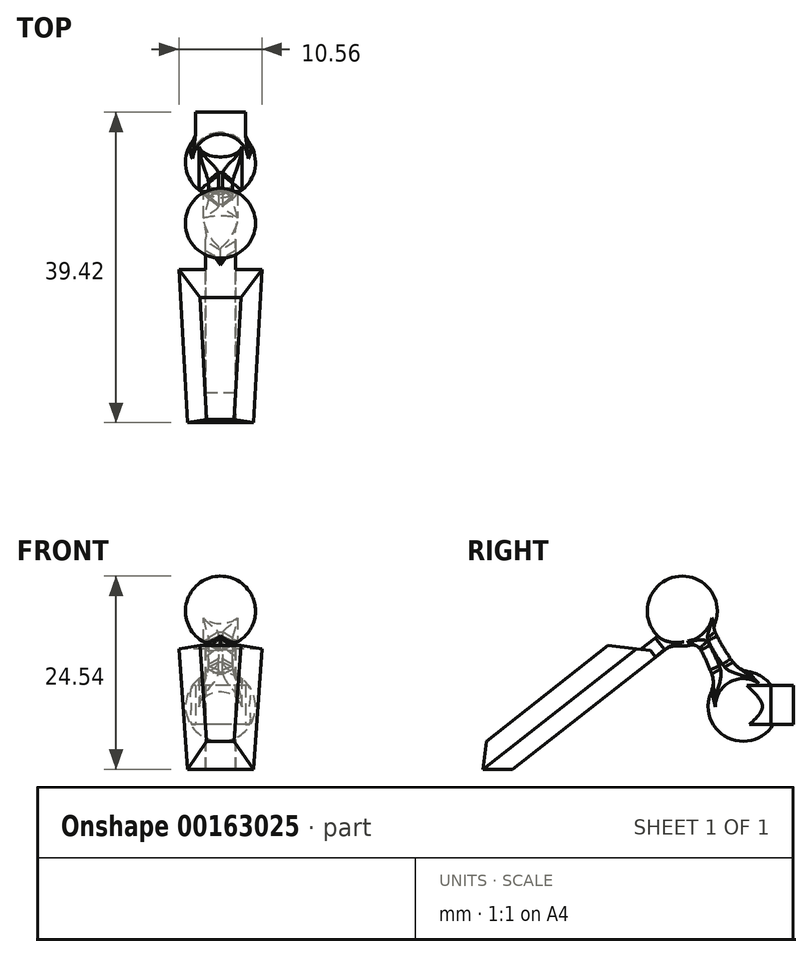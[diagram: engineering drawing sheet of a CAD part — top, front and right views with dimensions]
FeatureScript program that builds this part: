
annotation { "Feature Type Name" : "Feature", "Feature Type Description" : "" }
export const myFeature = defineFeature(function(context is Context, id is Id, definition is map)
    precondition{}
    {
        {
            var Q0;
            Q0=qCreatedBy(makeId("Right.planeOp"),FACE);
            var sketch = newSketch(context, id + "F0", { "sketchPlane" : qUnion([Q0])});
            skArc(sketch, "E0", {"start": v(4.45, 0) * mm, "mid": v(0, 4.45) * mm, "end": v(-4.45, 0) * mm});
            skLineSegment(sketch, "E1", {"start": v(-4.45, 0) * mm, "end": v(4.45, 0) * mm});
            skSolve(sketch);
        }
        {
            var Q0;
            Q0 = qSketchRegion(id + "F0", true);
            var Q1;
            Q1=sQuery(id+"F0.wireOp",EDGE,"E1");
            revolve(context, id + "F1", {"entities" : qUnion([Q0]), "axis" : qUnion([Q1]), "revolveType" : RevolveType.FULL});
        }
        {
            var Q0;
            Q0=qCreatedBy(makeId("Right.planeOp"),FACE);
            var sketch = newSketch(context, id + "F2", { "sketchPlane" : qUnion([Q0])});
            skArc(sketch, "E2", {"start": v(-3.29, 12.1) * mm, "mid": v(-7.73, 16.54) * mm, "end": v(-12.18, 12.1) * mm});
            skLineSegment(sketch, "E3", {"start": v(-16.01, 12.1) * mm, "end": v(-0.23, 12.1) * mm});
            skSolve(sketch);
        }
        {
            var Q0;
            Q0 = qSketchRegion(id + "F2", true);
            var Q1;
            Q1=sQuery(id+"F2.wireOp",EDGE,"E3");
            revolve(context, id + "F3", {"operationType" : NewBodyOperationType.ADD, "entities" : qUnion([Q0]), "axis" : qUnion([Q1]), "revolveType" : RevolveType.FULL});
        }
        {
            var Q0;
            Q0=qCreatedBy(makeId("Right.planeOp"),FACE);
            var sketch = newSketch(context, id + "F4", { "sketchPlane" : qUnion([Q0])});
            skLineSegment(sketch, "E4", {"start": v(0, 0) * mm, "end": v(-6.36, 11.76) * mm});
            skArc(sketch, "E5", {"start": v(-2.54, -2.6) * mm, "mid": v(-4.16, 4.59) * mm, "end": v(-7.92, 10.92) * mm});
            skArc(sketch, "E6.MirrorCS", {"start": v(3.56, 0.7) * mm, "mid": v(-1.56, 6) * mm, "end": v(-4.8, 12.6) * mm});
            skLineSegment(sketch, "E7", {"start": v(-2.54, -2.6) * mm, "end": v(3.56, 0.7) * mm});
            skLineSegment(sketch, "E8", {"start": v(-4.8, 12.6) * mm, "end": v(-7.92, 10.92) * mm});
            skPoint(sketch, "E9.orphan", {"position": v(-5.82, 18.71) * mm});
            skPoint(sketch, "E10.orphan", {"position": v(-12.46, 15.12) * mm});
            skSolve(sketch);
        }
        {
            var Q0;
            Q0 = qSketchRegion(id + "F4", true);
            extrude(context, id + "F5", {"entities" : qUnion([Q0]), "operationType" : NewBodyOperationType.ADD, "depth" : 3.05 * mm, "symmetric" : true});
        }
        {
            var Q0;
            Q0=qCreatedBy(makeId("Right.planeOp"),FACE);
            var sketch = newSketch(context, id + "F6", { "sketchPlane" : qUnion([Q0])});
            skLineSegment(sketch, "E11", {"start": v(-29.28, -8) * mm, "end": v(-7.9, 8.8) * mm});
            skLineSegment(sketch, "E12", {"start": v(-7.9, 8.8) * mm, "end": v(-9.42, 10.56) * mm});
            skLineSegment(sketch, "E13", {"start": v(-13.02, 7.73) * mm, "end": v(-33.05, -8) * mm});
            skLineSegment(sketch, "E14", {"start": v(-33.05, -8) * mm, "end": v(-29.28, -8) * mm});
            skLineSegment(sketch, "E15", {"start": v(-13.02, 7.73) * mm, "end": v(-9.42, 10.56) * mm});
            skSolve(sketch);
        }
        {
            var Q0;
            Q0 = qSketchRegion(id + "F6", true);
            extrude(context, id + "F7", {"entities" : qUnion([Q0]), "operationType" : NewBodyOperationType.ADD, "depth" : 3.8 * mm, "symmetric" : true});
        }
        {
            var Q0;
            Q0=qCreatedBy(makeId("Right.planeOp"),FACE);
            var sketch = newSketch(context, id + "F8", { "sketchPlane" : qUnion([Q0])});
            skLineSegment(sketch, "E16.bottom", {"start": v(3.52, -2.31) * mm, "end": v(6.37, -2.31) * mm});
            skLineSegment(sketch, "E16.top", {"start": v(3.52, 2.64) * mm, "end": v(6.37, 2.64) * mm});
            skLineSegment(sketch, "E16.left", {"start": v(3.52, -2.31) * mm, "end": v(3.52, 2.64) * mm});
            skLineSegment(sketch, "E17", {"start": v(6.37, 2.64) * mm, "end": v(6.37, -2.31) * mm});
            skSolve(sketch);
        }
        {
            var Q0;
            Q0 = qSketchRegion(id + "F8", true);
            extrude(context, id + "F9", {"entities" : qUnion([Q0]), "operationType" : NewBodyOperationType.ADD, "depth" : 3.17 * mm, "hasSecondDirection" : true, "secondDirectionOppositeDirection" : true, "secondDirectionDepth" : 3.17 * mm});
        }
        {
            var Q0;
            Q0=makeQuery(id+"F9.boolean.opBoolean","INTERSECT",EDGE,{"disambiguationData":[OD(1.0)],"derivedFrom":[makeQuery(id+"F1.opRevolve","SWEPT_FACE",FACE,{"disambiguationData":[OSD([sQuery(id+"F0.wireOp",EDGE,"E0")])]}),makeQuery(id+"F9.opExtrude","SWEPT_FACE",FACE,{"disambiguationData":[OSD([sQuery(id+"F8.wireOp",EDGE,"E16.left")])]})]});
            var Q1;
            Q1=makeQuery(id+"F9.boolean.opBoolean","INTERSECT",EDGE,{"disambiguationData":[OD(0.0)],"derivedFrom":[makeQuery(id+"F1.opRevolve","SWEPT_FACE",FACE,{"disambiguationData":[OSD([sQuery(id+"F0.wireOp",EDGE,"E0")])]}),makeQuery(id+"F9.opExtrude","SWEPT_FACE",FACE,{"disambiguationData":[OSD([sQuery(id+"F8.wireOp",EDGE,"E16.left")])]})]});
            fillet(context, id + "F10", {"entities" : qUnion([Q0, Q1]), "radius" : 5.08 * mm, "tangentPropagation" : true, "allowEdgeOverflow" : false});
        }
        {
            var Q0;
            Q0=makeQuery(id+"F5.boolean.opBoolean","INTERSECT",EDGE,{"derivedFrom":[makeQuery(id+"F1.opRevolve","SWEPT_FACE",FACE,{"disambiguationData":[OSD([sQuery(id+"F0.wireOp",EDGE,"E0")])]}),makeQuery(id+"F5.opExtrude","CAP_FACE",FACE,{"disambiguationData":[OSD([sQuery(id+"F4.wireOp",EDGE,"E5"),sQuery(id+"F4.wireOp",EDGE,"E6.MirrorCS"),sQuery(id+"F4.wireOp",EDGE,"E7"),sQuery(id+"F4.wireOp",EDGE,"5klLo1RB-Tudc-jpJ2-xB18-EwgxkBeXyRiw")])],"isStart":false})]});
            var Q1;
            Q1=makeQuery(id+"F5.boolean.opBoolean","INTERSECT",EDGE,{"derivedFrom":[makeQuery(id+"F1.opRevolve","SWEPT_FACE",FACE,{"disambiguationData":[OSD([sQuery(id+"F0.wireOp",EDGE,"E0")])]}),makeQuery(id+"F5.opExtrude","SWEPT_FACE",FACE,{"disambiguationData":[OSD([sQuery(id+"F4.wireOp",EDGE,"E6.MirrorCS")])]})]});
            var Q2;
            Q2=makeQuery(id+"F5.boolean.opBoolean","INTERSECT",EDGE,{"derivedFrom":[makeQuery(id+"F1.opRevolve","SWEPT_FACE",FACE,{"disambiguationData":[OSD([sQuery(id+"F0.wireOp",EDGE,"E0")])]}),makeQuery(id+"F5.opExtrude","CAP_FACE",FACE,{"disambiguationData":[OSD([sQuery(id+"F4.wireOp",EDGE,"E5"),sQuery(id+"F4.wireOp",EDGE,"E6.MirrorCS"),sQuery(id+"F4.wireOp",EDGE,"E7"),sQuery(id+"F4.wireOp",EDGE,"5klLo1RB-Tudc-jpJ2-xB18-EwgxkBeXyRiw")])],"isStart":true})]});
            var Q3;
            Q3=makeQuery(id+"F5.boolean.opBoolean","INTERSECT",EDGE,{"derivedFrom":[makeQuery(id+"F1.opRevolve","SWEPT_FACE",FACE,{"disambiguationData":[OSD([sQuery(id+"F0.wireOp",EDGE,"E0")])]}),makeQuery(id+"F5.opExtrude","SWEPT_FACE",FACE,{"disambiguationData":[OSD([sQuery(id+"F4.wireOp",EDGE,"E5")])]})]});
            fillet(context, id + "F11", {"entities" : qUnion([Q0, Q1, Q2, Q3]), "radius" : 3.05 * mm, "tangentPropagation" : true, "allowEdgeOverflow" : false});
        }
        {
            var Q0;
            Q0=makeQuery(id+"F5.boolean.opBoolean","INTERSECT",EDGE,{"derivedFrom":[makeQuery(id+"F3.opRevolve","SWEPT_FACE",FACE,{"disambiguationData":[OSD([sQuery(id+"F2.wireOp",EDGE,"E2")])]}),makeQuery(id+"F5.opExtrude","CAP_FACE",FACE,{"disambiguationData":[OSD([sQuery(id+"F4.wireOp",EDGE,"E5"),sQuery(id+"F4.wireOp",EDGE,"E6.MirrorCS"),sQuery(id+"F4.wireOp",EDGE,"E7"),sQuery(id+"F4.wireOp",EDGE,"5klLo1RB-Tudc-jpJ2-xB18-EwgxkBeXyRiw")])],"isStart":false})]});
            var Q1;
            Q1=makeQuery(id+"F5.boolean.opBoolean","INTERSECT",EDGE,{"derivedFrom":[makeQuery(id+"F3.opRevolve","SWEPT_FACE",FACE,{"disambiguationData":[OSD([sQuery(id+"F2.wireOp",EDGE,"E2")])]}),makeQuery(id+"F5.opExtrude","SWEPT_FACE",FACE,{"disambiguationData":[OSD([sQuery(id+"F4.wireOp",EDGE,"E6.MirrorCS")])]})]});
            var Q2;
            Q2=makeQuery(id+"F5.boolean.opBoolean","INTERSECT",EDGE,{"derivedFrom":[makeQuery(id+"F3.opRevolve","SWEPT_FACE",FACE,{"disambiguationData":[OSD([sQuery(id+"F2.wireOp",EDGE,"E2")])]}),makeQuery(id+"F5.opExtrude","CAP_FACE",FACE,{"disambiguationData":[OSD([sQuery(id+"F4.wireOp",EDGE,"E5"),sQuery(id+"F4.wireOp",EDGE,"E6.MirrorCS"),sQuery(id+"F4.wireOp",EDGE,"E7"),sQuery(id+"F4.wireOp",EDGE,"5klLo1RB-Tudc-jpJ2-xB18-EwgxkBeXyRiw")])],"isStart":true})]});
            var Q3;
            Q3=makeQuery(id+"F5.boolean.opBoolean","INTERSECT",EDGE,{"derivedFrom":[makeQuery(id+"F3.opRevolve","SWEPT_FACE",FACE,{"disambiguationData":[OSD([sQuery(id+"F2.wireOp",EDGE,"E2")])]}),makeQuery(id+"F5.opExtrude","SWEPT_FACE",FACE,{"disambiguationData":[OSD([sQuery(id+"F4.wireOp",EDGE,"E5")])]})]});
            fillet(context, id + "F12", {"entities" : qUnion([Q0, Q1, Q2, Q3]), "radius" : 1.27 * mm, "tangentPropagation" : true, "allowEdgeOverflow" : false});
        }
        {
            var Q0;
            Q0=makeQuery(id+"F5.opExtrude","CAP_EDGE",EDGE,{"disambiguationData":[OSD([sQuery(id+"F4.wireOp",EDGE,"E5")])],"isStart":false});
            var Q1;
            Q1=makeQuery(id+"F5.opExtrude","CAP_EDGE",EDGE,{"disambiguationData":[OSD([sQuery(id+"F4.wireOp",EDGE,"E6.MirrorCS")])],"isStart":false});
            var Q2;
            Q2=makeQuery(id+"F5.opExtrude","CAP_EDGE",EDGE,{"disambiguationData":[OSD([sQuery(id+"F4.wireOp",EDGE,"E6.MirrorCS")])],"isStart":true});
            var Q3;
            Q3=makeQuery(id+"F5.opExtrude","CAP_EDGE",EDGE,{"disambiguationData":[OSD([sQuery(id+"F4.wireOp",EDGE,"E5")])],"isStart":true});
            chamfer(context, id + "F13", {"entities" : qUnion([Q0, Q1, Q2, Q3]), "width" : 1.27 * mm, "tangentPropagation" : true});
        }
        {
            var Q0;
            Q0=makeQuery(id+"F7.boolean.opBoolean","INTERSECT",EDGE,{"derivedFrom":[makeQuery(id+"F3.opRevolve","SWEPT_FACE",FACE,{"disambiguationData":[OSD([sQuery(id+"F2.wireOp",EDGE,"E2")])]}),makeQuery(id+"F7.opExtrude","CAP_FACE",FACE,{"disambiguationData":[OSD([sQuery(id+"F6.wireOp",EDGE,"plxun01e-dWJy-UExp-mx6b-eehI6g0p5b8X"),sQuery(id+"F6.wireOp",EDGE,"1AYBgqKe-d7ER-K5aU-XKCM-2UsPj5wBxYO8"),sQuery(id+"F6.wireOp",EDGE,"E11"),sQuery(id+"F6.wireOp",EDGE,"E12")])],"isStart":false})]});
            var Q1;
            Q1=makeQuery(id+"F7.boolean.opBoolean","INTERSECT",EDGE,{"derivedFrom":[makeQuery(id+"F3.opRevolve","SWEPT_FACE",FACE,{"disambiguationData":[OSD([sQuery(id+"F2.wireOp",EDGE,"E2")])]}),makeQuery(id+"F7.opExtrude","SWEPT_FACE",FACE,{"disambiguationData":[OSD([sQuery(id+"F6.wireOp",EDGE,"1AYBgqKe-d7ER-K5aU-XKCM-2UsPj5wBxYO8")])]})]});
            var Q2;
            Q2=makeQuery(id+"F7.boolean.opBoolean","INTERSECT",EDGE,{"derivedFrom":[makeQuery(id+"F3.opRevolve","SWEPT_FACE",FACE,{"disambiguationData":[OSD([sQuery(id+"F2.wireOp",EDGE,"E2")])]}),makeQuery(id+"F7.opExtrude","SWEPT_FACE",FACE,{"disambiguationData":[OSD([sQuery(id+"F6.wireOp",EDGE,"E11")])]})]});
            var Q3;
            Q3=makeQuery(id+"F7.boolean.opBoolean","INTERSECT",EDGE,{"derivedFrom":[makeQuery(id+"F3.opRevolve","SWEPT_FACE",FACE,{"disambiguationData":[OSD([sQuery(id+"F2.wireOp",EDGE,"E2")])]}),makeQuery(id+"F7.opExtrude","CAP_FACE",FACE,{"disambiguationData":[OSD([sQuery(id+"F6.wireOp",EDGE,"plxun01e-dWJy-UExp-mx6b-eehI6g0p5b8X"),sQuery(id+"F6.wireOp",EDGE,"1AYBgqKe-d7ER-K5aU-XKCM-2UsPj5wBxYO8"),sQuery(id+"F6.wireOp",EDGE,"E11"),sQuery(id+"F6.wireOp",EDGE,"E12")])],"isStart":true})]});
            fillet(context, id + "F14", {"entities" : qUnion([Q0, Q1, Q2, Q3]), "radius" : 2.54 * mm, "tangentPropagation" : true, "allowEdgeOverflow" : false});
        }
        {
            var Q0;
            Q0=makeQuery(id+"F7.opExtrude","SWEPT_FACE",FACE,{"disambiguationData":[OSD([sQuery(id+"F6.wireOp",EDGE,"E13"),sQuery(id+"F6.wireOp",EDGE,"E15")])]});
            var sketch = newSketch(context, id + "F15", { "sketchPlane" : qUnion([Q0])});
            skLineSegment(sketch, "E18", {"start": v(0, -4.9) * mm, "end": v(5.33, -4.9) * mm});
            skLineSegment(sketch, "E19", {"start": v(5.33, -4.9) * mm, "end": v(4.18, -30.94) * mm});
            skLineSegment(sketch, "E20", {"start": v(4.18, -30.94) * mm, "end": v(0, -30.94) * mm});
            skLineSegment(sketch, "E21.MirrorCS", {"start": v(0, -4.9) * mm, "end": v(-5.33, -4.9) * mm});
            skLineSegment(sketch, "E22.MirrorCS", {"start": v(-5.33, -4.9) * mm, "end": v(-4.18, -30.94) * mm});
            skLineSegment(sketch, "E23.MirrorCS", {"start": v(-4.18, -30.94) * mm, "end": v(0, -30.94) * mm});
            skSolve(sketch);
        }
        {
            var Q0;
            Q0 = qSketchRegion(id + "F15", true);
            extrude(context, id + "F16", {"entities" : qUnion([Q0]), "operationType" : NewBodyOperationType.ADD, "depth" : 2.54 * mm});
        }
        {
            var Q0;
            Q0=makeQuery(id+"F16.opExtrude","CAP_EDGE",EDGE,{"disambiguationData":[OSD([sQuery(id+"F15.wireOp",EDGE,"E20"),sQuery(id+"F15.wireOp",EDGE,"E23.MirrorCS")])],"isStart":false});
            chamfer(context, id + "F17", {"entities" : qUnion([Q0]), "width" : 2.54 * mm, "tangentPropagation" : true});
        }
        {
            var Q0;
            Q0=makeQuery(id+"F16.opExtrude","CAP_EDGE",EDGE,{"disambiguationData":[OSD([sQuery(id+"F15.wireOp",EDGE,"E22.MirrorCS")])],"isStart":false});
            var Q1;
            Q1=makeQuery(id+"F16.opExtrude","CAP_EDGE",EDGE,{"disambiguationData":[OSD([sQuery(id+"F15.wireOp",EDGE,"E19")])],"isStart":false});
            chamfer(context, id + "F18", {"entities" : qUnion([Q0, Q1]), "width" : 2.54 * mm, "tangentPropagation" : true});
        }
        {
            var Q0;
            {var subQ0=sQuery(id+"F6.wireOp",EDGE,"E15");var subQ1=sQuery(id+"F6.wireOp",EDGE,"E13");Q0=makeQuery(id+"F16.boolean.opBoolean","SPLIT",EDGE,{"disambiguationData":[topologyDisambiguationEdgeConnected([makeQuery(id+"F16.opExtrude","CAP_FACE",FACE,{"disambiguationData":[OSD([sQuery(id+"F15.wireOp",EDGE,"E18"),sQuery(id+"F15.wireOp",EDGE,"E19"),sQuery(id+"F15.wireOp",EDGE,"E20"),sQuery(id+"F15.wireOp",EDGE,"E21.MirrorCS"),sQuery(id+"F15.wireOp",EDGE,"E22.MirrorCS"),sQuery(id+"F15.wireOp",EDGE,"E23.MirrorCS")])],"isStart":true})])],"derivedFrom":makeQuery(id+"F7.opExtrude","CAP_EDGE",EDGE,{"disambiguationData":[OSD([subQ1,subQ0])],"isStart":true})});}
            var Q1;
            {var subQ0=sQuery(id+"F6.wireOp",EDGE,"E15");var subQ1=sQuery(id+"F6.wireOp",EDGE,"E13");Q1=makeQuery(id+"F16.boolean.opBoolean","SPLIT",EDGE,{"disambiguationData":[topologyDisambiguationEdgeConnected([makeQuery(id+"F16.opExtrude","CAP_FACE",FACE,{"disambiguationData":[OSD([sQuery(id+"F15.wireOp",EDGE,"E18"),sQuery(id+"F15.wireOp",EDGE,"E19"),sQuery(id+"F15.wireOp",EDGE,"E20"),sQuery(id+"F15.wireOp",EDGE,"E21.MirrorCS"),sQuery(id+"F15.wireOp",EDGE,"E22.MirrorCS"),sQuery(id+"F15.wireOp",EDGE,"E23.MirrorCS")])],"isStart":true})])],"derivedFrom":makeQuery(id+"F7.opExtrude","CAP_EDGE",EDGE,{"disambiguationData":[OSD([subQ1,subQ0])],"isStart":false})});}
            chamfer(context, id + "F19", {"entities" : qUnion([Q0, Q1]), "width" : 2.3 * mm, "tangentPropagation" : true});
        }
        {
            var Q0;
            Q0=makeQuery(id+"F16.opExtrude","CAP_EDGE",EDGE,{"disambiguationData":[OSD([sQuery(id+"F15.wireOp",EDGE,"E18"),sQuery(id+"F15.wireOp",EDGE,"E21.MirrorCS")])],"isStart":false});
            chamfer(context, id + "F20", {"entities" : qUnion([Q0]), "width" : 3.8 * mm, "tangentPropagation" : true});
        }
    });
